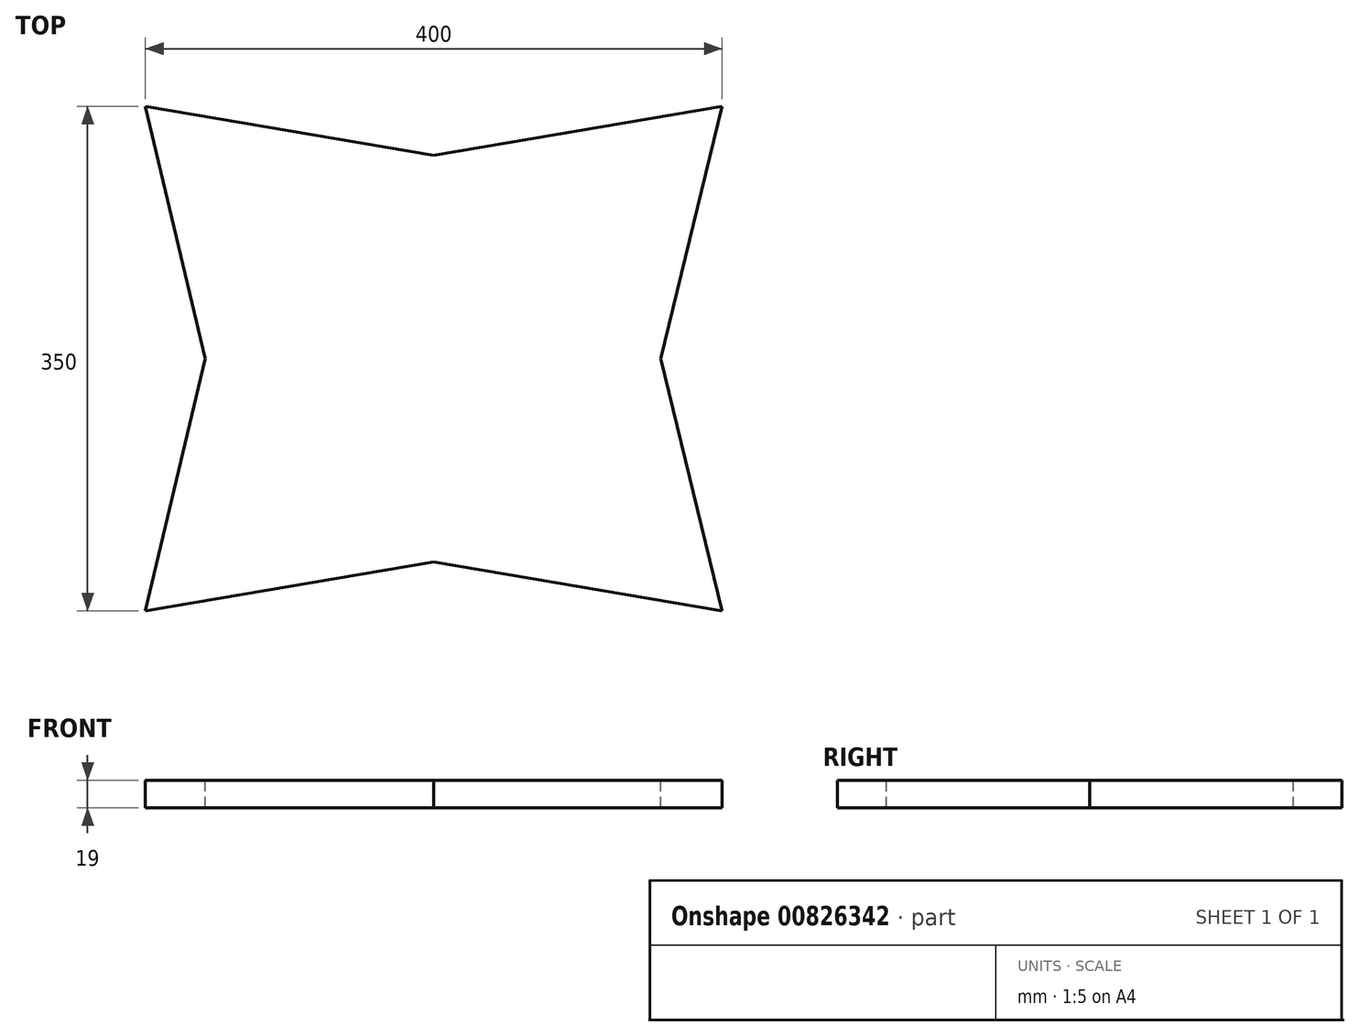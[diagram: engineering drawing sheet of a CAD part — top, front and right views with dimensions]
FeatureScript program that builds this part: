
annotation { "Feature Type Name" : "Feature", "Feature Type Description" : "" }
export const myFeature = defineFeature(function(context is Context, id is Id, definition is map)
    precondition{}
    {
        {
            var Q0;
            Q0=qCreatedBy(makeId("Top.planeOp"),FACE);
            var sketch = newSketch(context, id + "F0", { "sketchPlane" : qUnion([Q0])});
            skLineSegment(sketch, "E0.bottom", {"start": v(-200, 175) * mm, "end": v(200, 175) * mm});
            skLineSegment(sketch, "E0.top", {"start": v(-200, -175) * mm, "end": v(200, -175) * mm});
            skLineSegment(sketch, "E0.left", {"start": v(-200, 175) * mm, "end": v(-200, -175) * mm});
            skLineSegment(sketch, "E0.right", {"start": v(200, 175) * mm, "end": v(200, -175) * mm});
            skPoint(sketch, "E0.middle", {"position": v(0, 0) * mm});
            skSolve(sketch);
        }
        {
            var Q0;
            Q0=makeQuery(id+"F0.imprint","IMPRINT",FACE,{"disambiguationData":[TD([[makeQuery(id+"F0.imprint","IMPRINT",EDGE,{"derivedFrom":sQuery(id+"F0.wireOp",EDGE,"E0.bottom")}),-1.0]])]});
            extrude(context, id + "F1", {"entities" : qUnion([Q0]), "depth" : 19 * mm, "offsetDistance" : 25 * mm});
        }
        {
            var Q0;
            Q0=makeQuery(id+"F1.opExtrude","CAP_FACE",FACE,{"disambiguationData":[OSD([sQuery(id+"F0.wireOp",EDGE,"E0.bottom"),sQuery(id+"F0.wireOp",EDGE,"E0.top"),sQuery(id+"F0.wireOp",EDGE,"E0.left"),sQuery(id+"F0.wireOp",EDGE,"E0.right")])],"isStart":false});
            var sketch = newSketch(context, id + "F2", { "sketchPlane" : qUnion([Q0])});
            skLineSegment(sketch, "E1", {"start": v(-200, -175) * mm, "end": v(0, -141.07) * mm});
            skLineSegment(sketch, "E2", {"start": v(0, -141.07) * mm, "end": v(200, -175) * mm});
            skLineSegment(sketch, "E3", {"start": v(200, -175) * mm, "end": v(157.38, 0) * mm});
            skLineSegment(sketch, "E4", {"start": v(157.38, 0) * mm, "end": v(200, 175) * mm});
            skLineSegment(sketch, "E5", {"start": v(200, 175) * mm, "end": v(0, 141.07) * mm});
            skLineSegment(sketch, "E6", {"start": v(0, 141.07) * mm, "end": v(-200, 175) * mm});
            skLineSegment(sketch, "E7", {"start": v(-200, 175) * mm, "end": v(-158.47, 0) * mm});
            skLineSegment(sketch, "E8", {"start": v(-158.47, 0) * mm, "end": v(-200, -175) * mm});
            skSolve(sketch);
        }
        {
            var Q0;
            Q0=makeQuery(id+"F2.imprint","IMPRINT",FACE,{"disambiguationData":[TD([[makeQuery(id+"F2.imprint","IMPRINT",EDGE,{"derivedFrom":sQuery(id+"F2.wireOp",EDGE,"E7")}),-1.0]])]});
            var Q1;
            Q1=makeQuery(id+"F2.imprint","IMPRINT",FACE,{"disambiguationData":[TD([[makeQuery(id+"F2.imprint","IMPRINT",EDGE,{"derivedFrom":sQuery(id+"F2.wireOp",EDGE,"E1")}),-1.0]])]});
            var Q2;
            Q2=makeQuery(id+"F2.imprint","IMPRINT",FACE,{"disambiguationData":[TD([[makeQuery(id+"F2.imprint","IMPRINT",EDGE,{"derivedFrom":sQuery(id+"F2.wireOp",EDGE,"E3")}),-1.0]])]});
            var Q3;
            Q3=makeQuery(id+"F2.imprint","IMPRINT",FACE,{"disambiguationData":[TD([[makeQuery(id+"F2.imprint","IMPRINT",EDGE,{"derivedFrom":sQuery(id+"F2.wireOp",EDGE,"E5")}),-1.0]])]});
            extrude(context, id + "F3", {"entities" : qUnion([Q0, Q1, Q2, Q3]), "operationType" : NewBodyOperationType.REMOVE, "endBound" : BoundingType.THROUGH_ALL, "oppositeDirection" : true, "depth" : 25 * mm, "offsetDistance" : 25 * mm});
        }
    });
